# Revit family: SH-1717
name_source: partatom
category: Lighting Fixtures
revit_build: Autodesk Revit 2017 (Build: 20160225_1515(x64)
units: mm (PartAtom-declared; Revit-internal decimal feet)

## family parameters
Always vertical = No
Cut with Voids When Loaded = No
Light Source = Yes
OmniClass Number = 23.80.70.00
OmniClass Title = Lighting
Part Type = Normal
Room Calculation Point = No
Round Connector Dimension = Use Diameter
Shared = Yes
Work Plane-Based = Yes

## types (9) — shared parameters
Body Material = Aluminum
Color Filter = 16777215
Default Elevation = 121.9 cm
Dimming Lamp Color Temperature Shift = <None>
Flicker = Free Flicker
Height = 6.5 cm
IP = IP65
Lamp = LED
Manufacturer = SHOA
Model = SH-1717
Photometric Web File = CFAL930-7W 5000k.ies
Protection Class = Class I
Tilt Angle = 90.00°
Type medule = Power LED
URL = https://www.shoaco.com
Voltage/Frequency = 230V/50HZ
Website = www.shoaco.com
Width = 6.8 cm
consumption current = 0 A
wattage = 2 W

## per-type parameters (varying)
| type | Body color | color temperature |
| Sh-1717(White color-3000K-LED) | White color | 3000K |
| Sh-1717(White color-2000K-LED) | White color | 2000K |
| Sh-1717(White color-6500K-LED) | White color | 6500K |
| Sh-1717(Gray color-2000K-LED) | Gray color | 2000K |
| Sh-1717(Gray color-3000K-LED) | Gray color | 3000K |
| Sh-1717(Gray color-6500K-LED) | Gray color | 6500K |
| Sh-1717(Black color-2000K-LED) | Black color | 2000K |
| Sh-1717(Black color-3000K-LED) | Black color | 3000K |
| Sh-1717(Black color-6500K-LED) | Black color | 6500K |

## geometry (parser evidence)
native form markers: Sweep x13
no freeform markers — native parametric forms only
